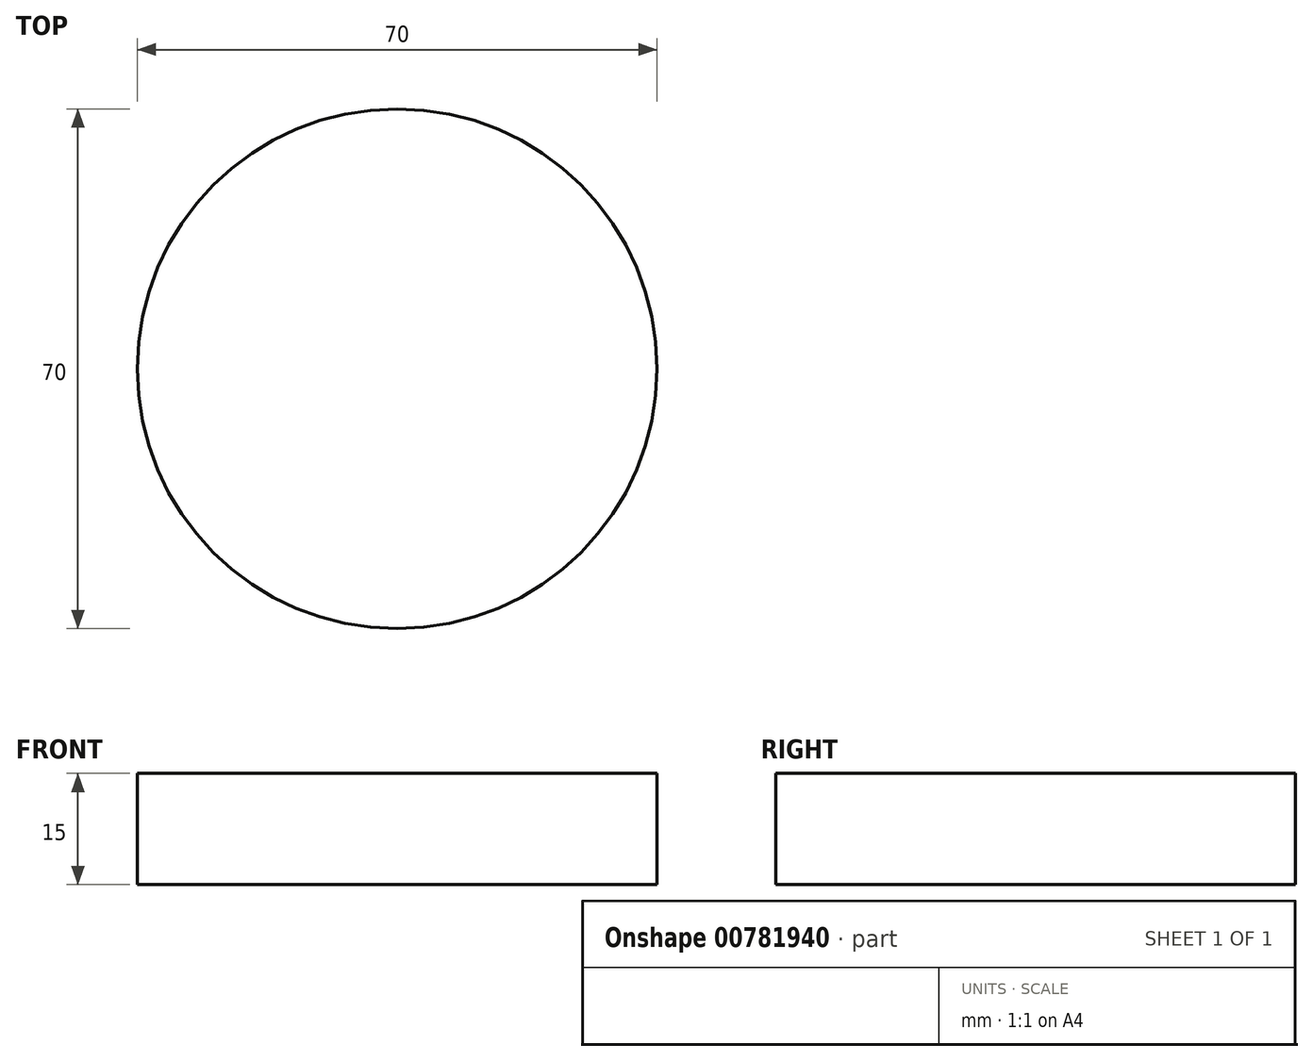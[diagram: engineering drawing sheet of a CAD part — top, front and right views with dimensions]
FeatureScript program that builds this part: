
annotation { "Feature Type Name" : "Feature", "Feature Type Description" : "" }
export const myFeature = defineFeature(function(context is Context, id is Id, definition is map)
    precondition{}
    {
        {
            var Q0;
            Q0=qCreatedBy(makeId("Front.planeOp"),FACE);
            var sketch = newSketch(context, id + "F0", { "sketchPlane" : qUnion([Q0])});
            skLineSegment(sketch, "E0.bottom", {"start": v(0, -5.05) * mm, "end": v(35, -5.05) * mm});
            skLineSegment(sketch, "E0.top", {"start": v(0, -20.05) * mm, "end": v(35, -20.05) * mm});
            skLineSegment(sketch, "E0.left", {"start": v(0, -5.05) * mm, "end": v(0, -20.05) * mm});
            skLineSegment(sketch, "E0.right", {"start": v(35, -5.05) * mm, "end": v(35, -20.05) * mm});
            skSolve(sketch);
        }
        {
            var Q0;
            Q0=makeQuery(id+"F0.imprint","IMPRINT",FACE,{"disambiguationData":[TD([[makeQuery(id+"F0.imprint","IMPRINT",EDGE,{"derivedFrom":sQuery(id+"F0.wireOp",EDGE,"E0.bottom")}),-1.0]])]});
            var Q1;
            Q1=sQuery(id+"F0.wireOp",EDGE,"E0.left");
            revolve(context, id + "F1", {"surfaceOperationType" : NewSurfaceOperationType.NEW, "entities" : qUnion([Q0]), "axis" : qUnion([Q1]), "revolveType" : RevolveType.FULL});
        }
    });
